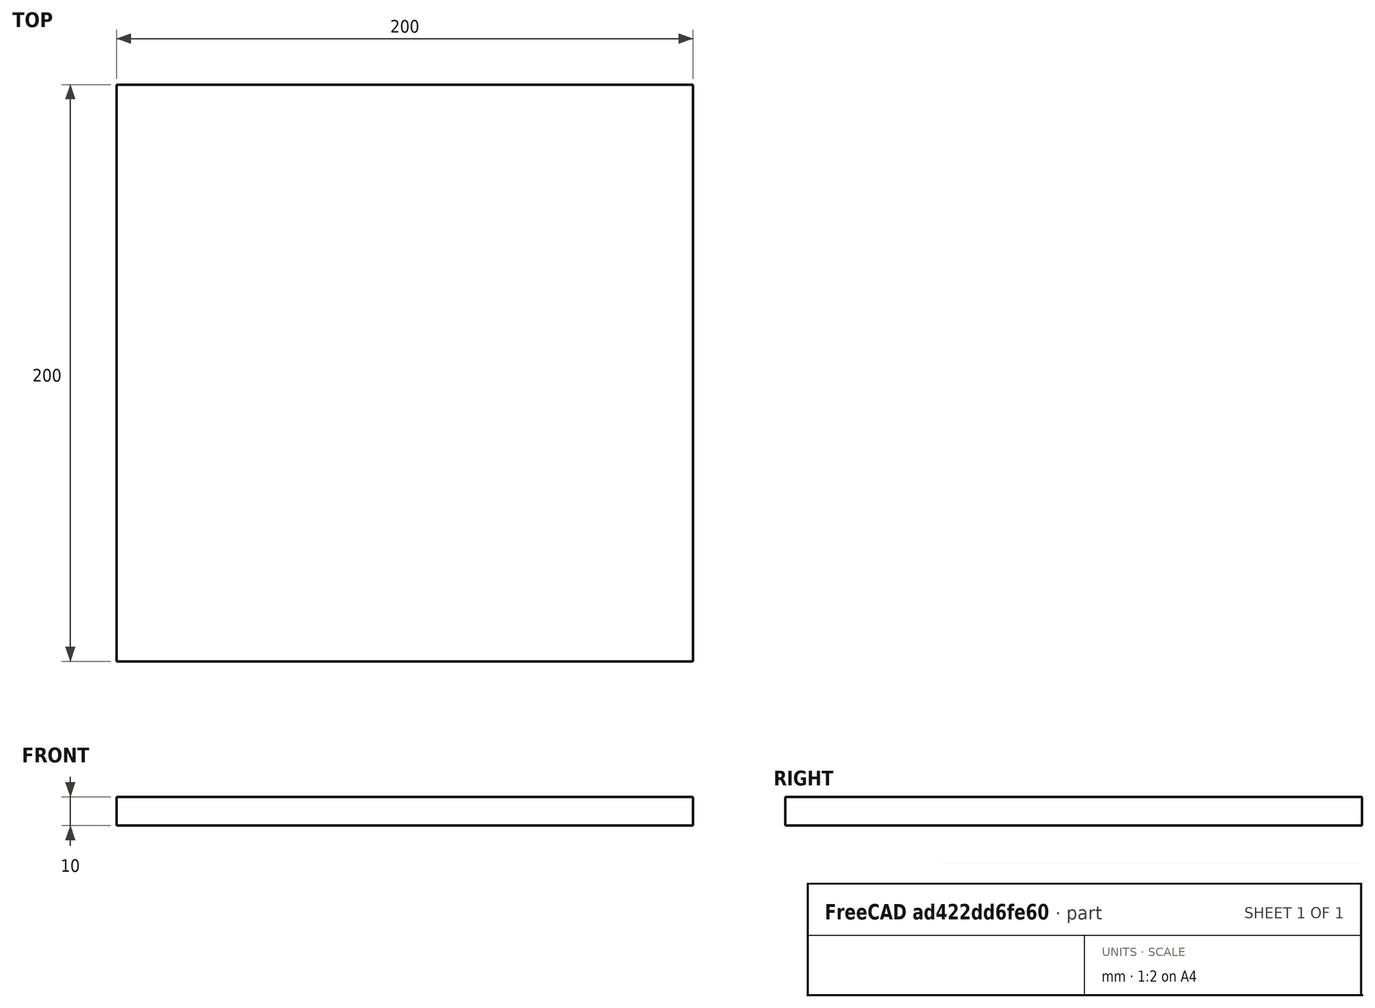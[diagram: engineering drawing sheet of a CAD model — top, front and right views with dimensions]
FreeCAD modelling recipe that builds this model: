
FCSTD DOCUMENT  (FreeCAD 0.19R24276 (Git))
Label: bldc_holder_p1_200x200x10
License: All rights reserved
LicenseURL: http://en.wikipedia.org/wiki/All_rights_reserved
objects: Sketcher::SketchObject×1, PartDesign::Pad×1, PartDesign::Body×1
note: 4 computed .brp shape members not serialized (recipe doc carries the construction recipe); baked Part::Feature solids carry a one-line shape summary decoded from their .brp

FEATURE [Sketcher::SketchObject] Sketch
  FullyConstrained = true
  MapMode = 5
  Support = -> [XY_Plane]
  sketch-geometry (4):
    g0: LineSegment StartX=0 StartY=0 StartZ=0 EndX=200 EndY=0 EndZ=0
    g1: LineSegment StartX=200 StartY=0 StartZ=0 EndX=200 EndY=200 EndZ=0
    g2: LineSegment StartX=200 StartY=200 StartZ=0 EndX=0 EndY=200 EndZ=0
    g3: LineSegment StartX=0 StartY=200 StartZ=0 EndX=0 EndY=0 EndZ=0
  constraints (11):
    c: Coincident(g0,g1)
    c: Coincident(g1,g2)
    c: Coincident(g2,g3)
    c: Coincident(g3,g0)
    c: Horizontal(g0)
    c: Horizontal(g2)
    c: Vertical(g1)
    c: Vertical(g3)
    c: Coincident(g0,g-1)
    c: Equal(g1,g2)
    c: DistanceX(g0,g0) = 200
FEATURE [PartDesign::Pad] Pad
  Direction = (1,1,1)
  Length = 10
  Length2 = 100
  Profile = -> Sketch
  Type = 0
FEATURE [PartDesign::Body] Body
  Group = -> [Sketch,Pad]
  Origin = -> Origin
  Tip = -> Pad
